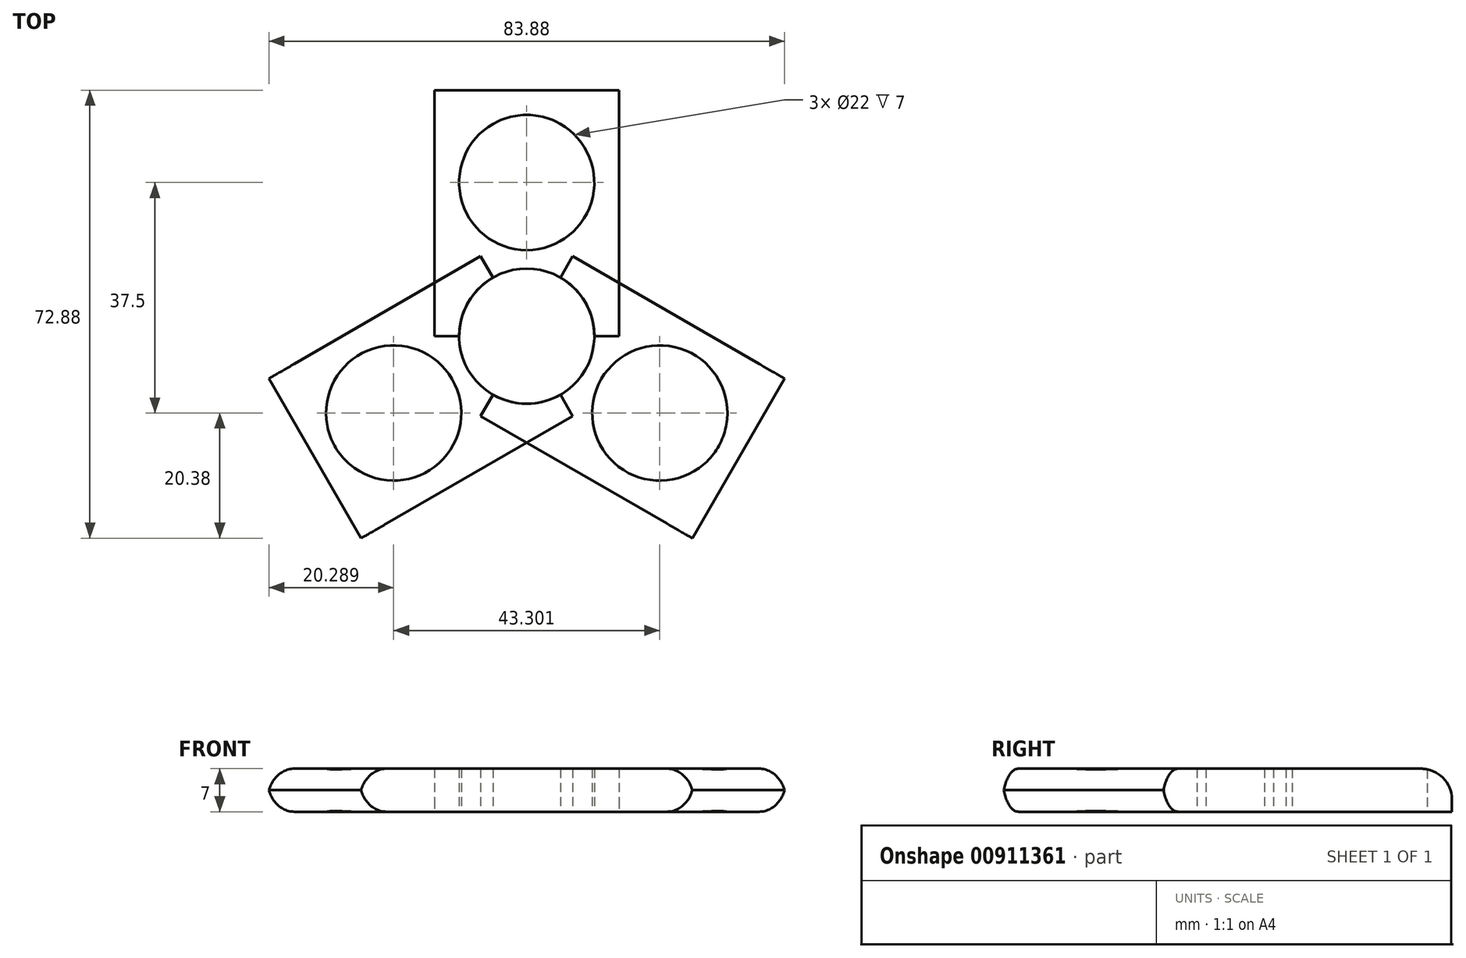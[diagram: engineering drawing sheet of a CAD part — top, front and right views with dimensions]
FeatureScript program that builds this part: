
annotation { "Feature Type Name" : "Feature", "Feature Type Description" : "" }
export const myFeature = defineFeature(function(context is Context, id is Id, definition is map)
    precondition{}
    {
        {
            var Q0;
            Q0=qCreatedBy(makeId("Top.planeOp"),FACE);
            var sketch = newSketch(context, id + "F0", { "sketchPlane" : qUnion([Q0])});
            skCircle(sketch, "E0", {"center": v(0, 0) * mm, "radius": 11 * mm});
            skLineSegment(sketch, "E1.bottom", {"start": v(0, 0) * mm, "end": v(15, 0) * mm});
            skLineSegment(sketch, "E1.top", {"start": v(0, 40) * mm, "end": v(15, 40) * mm});
            skLineSegment(sketch, "E1.left", {"start": v(0, 0) * mm, "end": v(0, 40) * mm});
            skLineSegment(sketch, "E1.right", {"start": v(15, 0) * mm, "end": v(15, 40) * mm});
            skLineSegment(sketch, "E2.bottom", {"start": v(0, 0) * mm, "end": v(-15, 0) * mm});
            skLineSegment(sketch, "E2.top", {"start": v(0, 40) * mm, "end": v(-15, 40) * mm});
            skLineSegment(sketch, "E2.right", {"start": v(-15, 0) * mm, "end": v(-15, 40) * mm});
            skLineSegment(sketch, "E3", {"start": v(0, 25) * mm, "end": v(0, 11) * mm});
            skCircle(sketch, "E4", {"center": v(0, 25) * mm, "radius": 11 * mm});
            skSolve(sketch);
        }
        {
            var Q0;
            {var subQ1=sQuery(id+"F0.wireOp",EDGE,"E2.top");Q0=makeQuery(id+"F0.imprint","IMPRINT",FACE,{"disambiguationData":[TD([[makeQuery(id+"F0.imprint","IMPRINT",EDGE,{"derivedFrom":subQ1}),1.0]])]});}
            var Q1;
            {var subQ10=sQuery(id+"F0.wireOp",EDGE,"E1.top");Q1=makeQuery(id+"F0.imprint","IMPRINT",FACE,{"disambiguationData":[TD([[makeQuery(id+"F0.imprint","IMPRINT",EDGE,{"derivedFrom":subQ10}),-1.0]])]});}
            extrude(context, id + "F1", {"entities" : qUnion([Q0, Q1]), "depth" : 7 * mm, "offsetDistance" : 25 * mm});
        }
        {
            var Q0;
            Q0=qCreatedBy(makeId("Front.planeOp"),FACE);
            var sketch = newSketch(context, id + "F2", { "sketchPlane" : qUnion([Q0])});
            skLineSegment(sketch, "E5", {"start": v(0, 0) * mm, "end": v(0, 40.07) * mm});
            skSolve(sketch);
        }
        {
            var Q0;
            Q0=makeQuery(id+"F1.opExtrude","SWEPT_BODY",BODY,{"disambiguationData":[OSD([sQuery(id+"F0.wireOp",EDGE,"E0"),sQuery(id+"F0.wireOp",EDGE,"E1.bottom"),sQuery(id+"F0.wireOp",EDGE,"E1.top"),sQuery(id+"F0.wireOp",EDGE,"E1.right"),sQuery(id+"F0.wireOp",EDGE,"E2.bottom"),sQuery(id+"F0.wireOp",EDGE,"E2.top"),sQuery(id+"F0.wireOp",EDGE,"E2.right"),sQuery(id+"F0.wireOp",EDGE,"E4")])]});
            var Q1;
            Q1=sQuery(id+"F2.wireOp",EDGE,"E5");
            var Q2;
            Q2=sQuery(id+"F2.wireOp",EDGE,"E5");
            transform(context, id + "F3", {"entities" : qUnion([Q0]), "transformType" : TransformType.ROTATION, "transformAxis" : qUnion([Q2]), "angle" : 120 * degree, "makeCopy" : true});
        }
        {
            var Q0;
            Q0=qCreatedBy(makeId("Front.planeOp"),FACE);
            var sketch = newSketch(context, id + "F4", { "sketchPlane" : qUnion([Q0])});
            skLineSegment(sketch, "E6", {"start": v(0, 0) * mm, "end": v(0, 24.94) * mm});
            skSolve(sketch);
        }
        {
            var Q0;
            Q0=makeQuery(id+"F3.opPattern","COPY",BODY,{"derivedFrom":makeQuery(id+"F1.opExtrude","SWEPT_BODY",BODY,{"disambiguationData":[OSD([sQuery(id+"F0.wireOp",EDGE,"E0"),sQuery(id+"F0.wireOp",EDGE,"E1.bottom"),sQuery(id+"F0.wireOp",EDGE,"E1.top"),sQuery(id+"F0.wireOp",EDGE,"E1.right"),sQuery(id+"F0.wireOp",EDGE,"E2.bottom"),sQuery(id+"F0.wireOp",EDGE,"E2.top"),sQuery(id+"F0.wireOp",EDGE,"E2.right"),sQuery(id+"F0.wireOp",EDGE,"E4")])]}),"instanceName":"1"});
            var Q1;
            Q1=sQuery(id+"F4.wireOp",EDGE,"E6");
            transform(context, id + "F5", {"entities" : qUnion([Q0]), "transformType" : TransformType.ROTATION, "transformAxis" : qUnion([Q1]), "angle" : 120 * degree, "makeCopy" : true});
        }
        {
            var Q0;
            Q0=makeQuery(id+"F3.opPattern","COPY",EDGE,{"derivedFrom":makeQuery(id+"F1.opExtrude","CAP_EDGE",EDGE,{"disambiguationData":[OSD([sQuery(id+"F0.wireOp",EDGE,"E1.top"),sQuery(id+"F0.wireOp",EDGE,"E2.top")])],"isStart":false}),"instanceName":"1"});
            var Q1;
            Q1=makeQuery(id+"F3.opPattern","COPY",EDGE,{"derivedFrom":makeQuery(id+"F1.opExtrude","CAP_EDGE",EDGE,{"disambiguationData":[OSD([sQuery(id+"F0.wireOp",EDGE,"E1.top"),sQuery(id+"F0.wireOp",EDGE,"E2.top")])],"isStart":true}),"instanceName":"1"});
            var Q2;
            Q2=makeQuery(id+"F5.opPattern","COPY",EDGE,{"derivedFrom":makeQuery(id+"F3.opPattern","COPY",EDGE,{"derivedFrom":makeQuery(id+"F1.opExtrude","CAP_EDGE",EDGE,{"disambiguationData":[OSD([sQuery(id+"F0.wireOp",EDGE,"E1.top"),sQuery(id+"F0.wireOp",EDGE,"E2.top")])],"isStart":true}),"instanceName":"1"}),"instanceName":"1"});
            var Q3;
            Q3=makeQuery(id+"F5.opPattern","COPY",EDGE,{"derivedFrom":makeQuery(id+"F3.opPattern","COPY",EDGE,{"derivedFrom":makeQuery(id+"F1.opExtrude","CAP_EDGE",EDGE,{"disambiguationData":[OSD([sQuery(id+"F0.wireOp",EDGE,"E1.top"),sQuery(id+"F0.wireOp",EDGE,"E2.top")])],"isStart":false}),"instanceName":"1"}),"instanceName":"1"});
            var Q4;
            Q4=makeQuery(id+"F1.opExtrude","CAP_EDGE",EDGE,{"disambiguationData":[OSD([sQuery(id+"F0.wireOp",EDGE,"E1.top"),sQuery(id+"F0.wireOp",EDGE,"E2.top")])],"isStart":false});
            fillet(context, id + "F6", {"entities" : qUnion([Q0, Q1, Q2, Q3, Q4]), "radius" : 5 * mm, "tangentPropagation" : true, "allowEdgeOverflow" : false});
        }
    });
